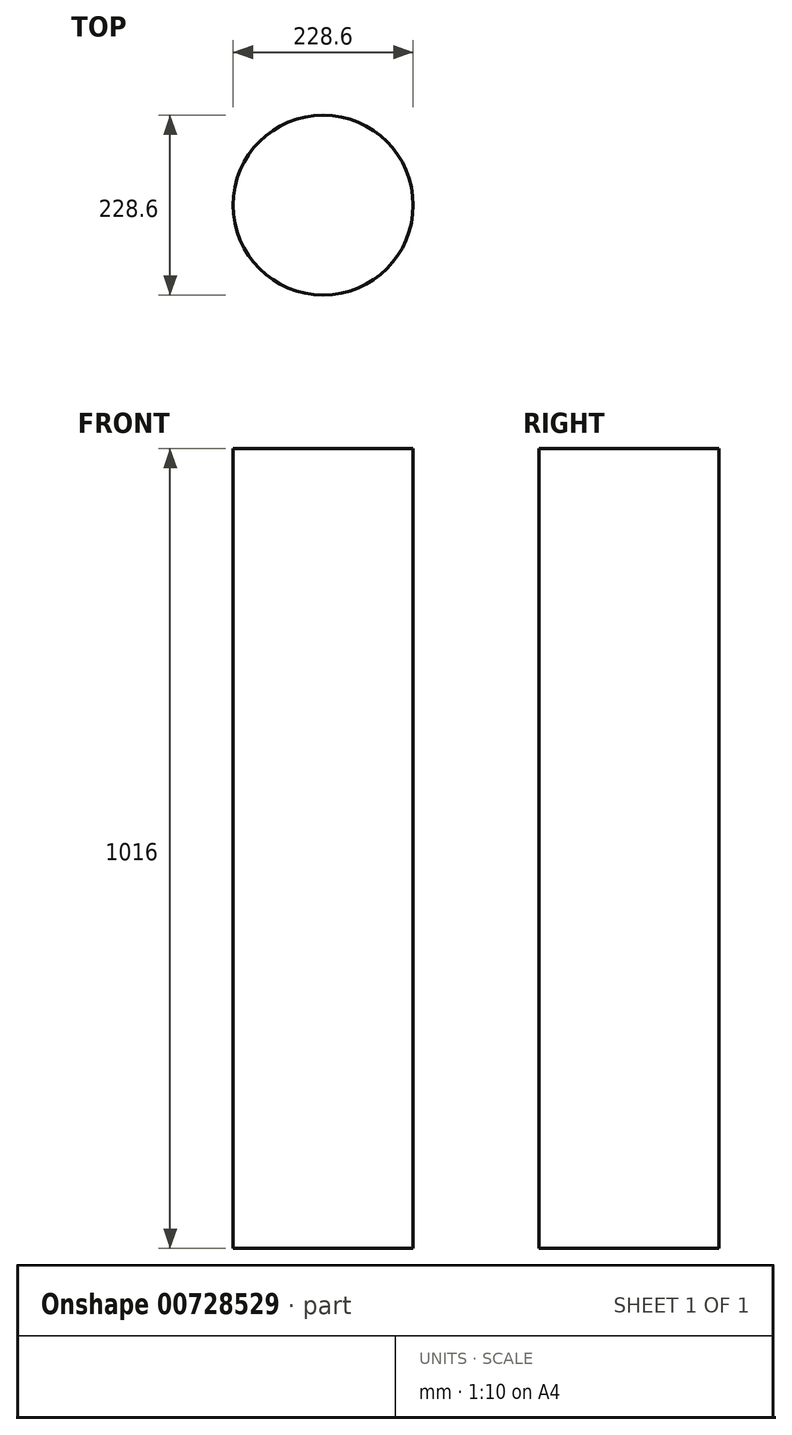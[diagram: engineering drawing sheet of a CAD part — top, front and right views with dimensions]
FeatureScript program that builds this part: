
annotation { "Feature Type Name" : "Feature", "Feature Type Description" : "" }
export const myFeature = defineFeature(function(context is Context, id is Id, definition is map)
    precondition{}
    {
        {
            var Q0;
            Q0=qCreatedBy(makeId("Top.planeOp"),FACE);
            var sketch = newSketch(context, id + "F0", { "sketchPlane" : qUnion([Q0])});
            skCircle(sketch, "E0", {"center": v(0, 0) * mm, "radius": 114.3 * mm});
            skSolve(sketch);
        }
        {
            var Q0;
            Q0 = qSketchRegion(id + "F0", true);
            extrude(context, id + "F1", {"entities" : qUnion([Q0]), "depth" : 1016 * mm, "offsetDistance" : 25.4 * mm});
        }
    });
